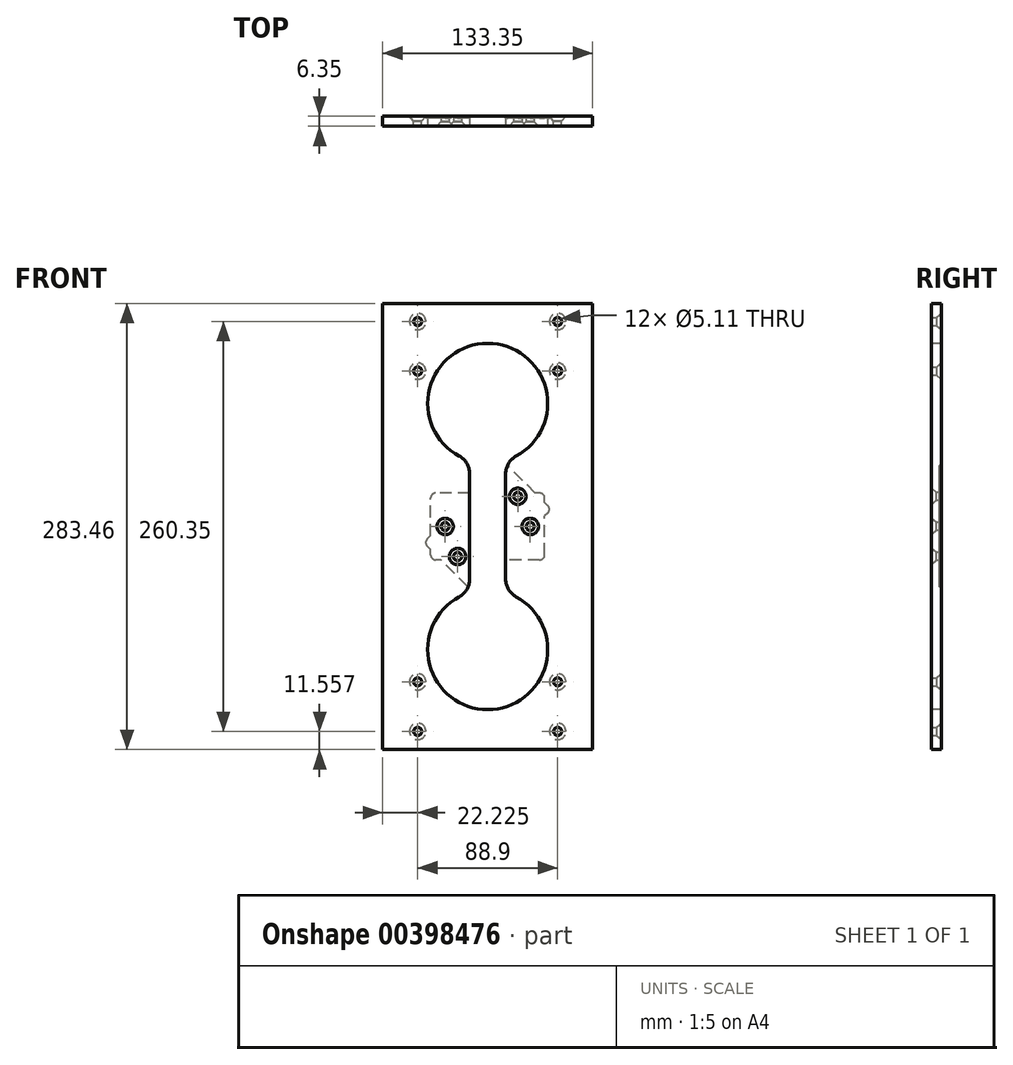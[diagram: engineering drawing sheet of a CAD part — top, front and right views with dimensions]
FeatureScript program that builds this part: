
annotation { "Feature Type Name" : "Feature", "Feature Type Description" : "" }
export const myFeature = defineFeature(function(context is Context, id is Id, definition is map)
    precondition{}
    {
        {
            var Q0;
            Q0=qCreatedBy(makeId("Top.planeOp"),FACE);
            var sketch = newSketch(context, id + "F0", { "sketchPlane" : qUnion([Q0])});
            skLineSegment(sketch, "E0.bottom", {"start": v(0, 0) * mm, "end": v(133.35, 0) * mm});
            skLineSegment(sketch, "E0.top", {"start": v(0, 6.35) * mm, "end": v(133.35, 6.35) * mm});
            skLineSegment(sketch, "E0.left", {"start": v(0, 0) * mm, "end": v(0, 6.35) * mm});
            skLineSegment(sketch, "E0.right", {"start": v(133.35, 0) * mm, "end": v(133.35, 6.35) * mm});
            skSolve(sketch);
        }
        {
            var Q0;
            Q0 = qSketchRegion(id + "F0", true);
            extrude(context, id + "F1", {"entities" : qUnion([Q0]), "depth" : 283.46 * mm});
        }
        {
            var Q0;
            Q0=qCreatedBy(makeId("Top.planeOp"),FACE);
            cPlane(context, id + "F2", {"entities" : qUnion([Q0]), "cplaneType" : CPlaneType.OFFSET, "offset" : ((10.25 + 2 * .455) / 2) * mm, "width" : 152.4 * mm, "height" : 152.4 * mm});
        }
        {
            var Q0;
            Q0=makeQuery(id+"F1.opExtrude","SWEPT_FACE",FACE,{"disambiguationData":[OSD([sQuery(id+"F0.wireOp",EDGE,"E0.bottom")])]});
            var sketch = newSketch(context, id + "F3", { "sketchPlane" : qUnion([Q0])});
            skPoint(sketch, "E1", {"position": v(111.13, 11.56) * mm});
            skPoint(sketch, "E2", {"position": v(22.23, 11.56) * mm});
            skPoint(sketch, "E3", {"position": v(111.13, 271.9) * mm});
            skPoint(sketch, "E4", {"position": v(22.22, 271.9) * mm});
            skLineSegment(sketch, "E5", {"start": v(111.13, 271.9) * mm, "end": v(111.13, 11.56) * mm, "construction": true});
            skLineSegment(sketch, "E6", {"start": v(22.23, 11.56) * mm, "end": v(22.22, 271.9) * mm, "construction": true});
            skPoint(sketch, "E7", {"position": v(111.13, 43.05) * mm});
            skPoint(sketch, "E8", {"position": v(22.23, 43.05) * mm});
            skPoint(sketch, "E9", {"position": v(111.13, 240.41) * mm});
            skPoint(sketch, "E10", {"position": v(22.22, 240.41) * mm});
            skSolve(sketch);
        }
        {
            var Q0;
            {var subQ0=sQuery(id+"F0.wireOp",EDGE,"E0.bottom");Q0=makeQuery(id+"F3.imprint","IMPRINT",FACE,{"disambiguationData":[TD([[makeQuery(id+"F3.imprint","IMPRINT",EDGE,{"derivedFrom":makeQuery(id+"F1.opExtrude","CAP_EDGE",EDGE,{"disambiguationData":[OSD([subQ0])],"isStart":true})}),1.0]])]});}
            var sketch = newSketch(context, id + "F4", { "sketchPlane" : qUnion([Q0])});
            skLineSegment(sketch, "E11.bottom", {"start": v(33.4, 162.43) * mm, "end": v(99.95, 162.43) * mm, "construction": true});
            skLineSegment(sketch, "E11.top", {"start": v(33.4, 121.03) * mm, "end": v(99.95, 121.03) * mm, "construction": true});
            skLineSegment(sketch, "E11.left", {"start": v(31.12, 160.4) * mm, "end": v(31.12, 123.06) * mm, "construction": true});
            skLineSegment(sketch, "E11.right", {"start": v(102.24, 160.4) * mm, "end": v(102.24, 123.06) * mm, "construction": true});
            skLineSegment(sketch, "E12", {"start": v(99.95, 162.43) * mm, "end": v(102.24, 160.4) * mm, "construction": true});
            skLineSegment(sketch, "E13", {"start": v(102.23, 123.06) * mm, "end": v(99.95, 121.03) * mm, "construction": true});
            skLineSegment(sketch, "E14", {"start": v(31.12, 123.06) * mm, "end": v(33.4, 121.03) * mm, "construction": true});
            skLineSegment(sketch, "E15", {"start": v(31.12, 160.4) * mm, "end": v(33.4, 162.43) * mm, "construction": true});
            skLineSegment(sketch, "E16", {"start": v(0, 141.73) * mm, "end": v(133.35, 141.73) * mm, "construction": true});
            skLineSegment(sketch, "E17", {"start": v(66.68, 121.03) * mm, "end": v(66.68, 162.43) * mm, "construction": true});
            skPoint(sketch, "E18", {"position": v(39.66, 141.73) * mm});
            skPoint(sketch, "E19", {"position": v(93.7, 141.73) * mm});
            skPoint(sketch, "E20.1.0", {"position": v(47.57, 122.63) * mm});
            skPoint(sketch, "E20.1.1", {"position": v(85.78, 160.84) * mm});
            skPoint(sketch, "E20.center", {"position": v(66.68, 141.73) * mm});
            skLineSegment(sketch, "E20.anchor1", {"start": v(66.68, 141.73) * mm, "end": v(39.66, 141.73) * mm, "construction": true});
            skLineSegment(sketch, "E20.anchor2", {"start": v(66.68, 141.73) * mm, "end": v(47.57, 122.63) * mm, "construction": true});
            skSolve(sketch);
        }
        {
            var Q0;
            Q0=makeQuery(id+"F1.opExtrude","SWEPT_FACE",FACE,{"disambiguationData":[OSD([sQuery(id+"F0.wireOp",EDGE,"E0.top")])]});
            var sketch = newSketch(context, id + "F5", { "sketchPlane" : qUnion([Q0])});
            skLineSegment(sketch, "E21.bottom", {"start": v(-99.7, 120.52) * mm, "end": v(-75.08, 120.52) * mm});
            skLineSegment(sketch, "E21.top", {"start": v(-99.7, 162.94) * mm, "end": v(-96.89, 162.94) * mm});
            skLineSegment(sketch, "E21.left", {"start": v(-102.87, 123.7) * mm, "end": v(-102.87, 148.31) * mm});
            skLineSegment(sketch, "E21.right", {"start": v(-30.48, 123.7) * mm, "end": v(-30.48, 126.97) * mm});
            skPoint(sketch, "E22.visualSharp", {"position": v(-102.87, 162.94) * mm});
            skArc(sketch, "E22.filletArc", {"start": v(-99.7, 162.94) * mm, "mid": v(-101.94, 162.01) * mm, "end": v(-102.87, 159.77) * mm});
            skArc(sketch, "E23.filletArc", {"start": v(-102.87, 123.7) * mm, "mid": v(-101.94, 121.45) * mm, "end": v(-99.7, 120.52) * mm});
            skPoint(sketch, "E24.visualSharp", {"position": v(-30.48, 162.94) * mm});
            skArc(sketch, "E24.filletArc", {"start": v(-30.48, 159.77) * mm, "mid": v(-31.4, 162.01) * mm, "end": v(-33.66, 162.94) * mm});
            skArc(sketch, "E25.filletArc", {"start": v(-33.66, 120.52) * mm, "mid": v(-31.4, 121.45) * mm, "end": v(-30.48, 123.7) * mm});
            skPoint(sketch, "E26", {"position": v(-66.27, 141.8) * mm});
            skLineSegment(sketch, "E27.1.0", {"start": v(-74.95, 180.38) * mm, "end": v(-57.51, 162.94) * mm});
            skLineSegment(sketch, "E27.1.1", {"start": v(-53.76, 103.7) * mm, "end": v(-36.93, 120.52) * mm});
            skPoint(sketch, "E27.1.2", {"position": v(-77.2, 182.63) * mm});
            skLineSegment(sketch, "E27.1.3", {"start": v(-104.95, 154.88) * mm, "end": v(-102.87, 156.96) * mm});
            skPoint(sketch, "E27.1.5", {"position": v(-26.01, 131.44) * mm});
            skLineSegment(sketch, "E27.1.6", {"start": v(-104.95, 150.39) * mm, "end": v(-102.87, 148.31) * mm});
            skArc(sketch, "E27.1.7", {"start": v(-104.95, 154.88) * mm, "mid": v(-105.88, 152.63) * mm, "end": v(-104.95, 150.39) * mm});
            skArc(sketch, "E27.1.8", {"start": v(-58.25, 103.7) * mm, "mid": v(-56, 102.76) * mm, "end": v(-53.76, 103.7) * mm});
            skArc(sketch, "E27.1.9", {"start": v(-74.95, 180.38) * mm, "mid": v(-77.2, 181.31) * mm, "end": v(-79.44, 180.38) * mm});
            skArc(sketch, "E27.1.10", {"start": v(-28.26, 129.2) * mm, "mid": v(-27.33, 131.44) * mm, "end": v(-28.26, 133.69) * mm});
            skLineSegment(sketch, "E27.anchor1", {"start": v(-66.27, 141.8) * mm, "end": v(-99.7, 120.52) * mm, "construction": true});
            skLineSegment(sketch, "E27.anchor2", {"start": v(-66.27, 141.8) * mm, "end": v(-104.95, 150.39) * mm, "construction": true});
            skLineSegment(sketch, "E28.trimOffspring", {"start": v(-57.51, 162.94) * mm, "end": v(-33.66, 162.94) * mm});
            skLineSegment(sketch, "E29.trimOffspring", {"start": v(-30.48, 135.91) * mm, "end": v(-28.26, 133.69) * mm});
            skLineSegment(sketch, "E30.trimOffspring", {"start": v(-30.48, 135.91) * mm, "end": v(-30.48, 159.77) * mm});
            skLineSegment(sketch, "E31.trimOffspring", {"start": v(-36.93, 120.52) * mm, "end": v(-33.66, 120.52) * mm});
            skLineSegment(sketch, "E32.trimOffspring", {"start": v(-30.48, 126.97) * mm, "end": v(-28.26, 129.2) * mm});
            skLineSegment(sketch, "E33.trimOffspring", {"start": v(-75.08, 120.52) * mm, "end": v(-58.25, 103.7) * mm});
            skLineSegment(sketch, "E34.trimOffspring", {"start": v(-102.87, 156.96) * mm, "end": v(-102.87, 159.77) * mm});
            skLineSegment(sketch, "E35.trimOffspring", {"start": v(-96.89, 162.94) * mm, "end": v(-79.44, 180.38) * mm});
            skSolve(sketch);
        }
        {
            var Q0;
            Q0 = qSketchRegion(id + "F5", true);
            extrude(context, id + "F6", {"entities" : qUnion([Q0]), "operationType" : NewBodyOperationType.REMOVE, "oppositeDirection" : true, "depth" : 1.27 * mm});
        }
        {
            var Q0;
            Q0=sQuery(id+"F4.wireOp",VERTEX,"E18");
            var Q1;
            Q1=sQuery(id+"F4.wireOp",VERTEX,"E19");
            var Q2;
            Q2=sQuery(id+"F4.wireOp",VERTEX,"E20.1.1");
            var Q3;
            Q3=sQuery(id+"F4.wireOp",VERTEX,"E20.1.0");
            var Q4;
            Q4=makeQuery(id+"F1.opExtrude","SWEPT_BODY",BODY,{"disambiguationData":[OSD([sQuery(id+"F0.wireOp",EDGE,"E0.bottom"),sQuery(id+"F0.wireOp",EDGE,"E0.top"),sQuery(id+"F0.wireOp",EDGE,"E0.left"),sQuery(id+"F0.wireOp",EDGE,"E0.right")])]});
            hole(context, id + "F7", {"style" : HoleStyle.C_SINK, "endStyle" : HoleEndStyle.THROUGH, "standardTappedOrClearance" : lookupTablePath({ "standard" : "ANSI", "fit" : "Normal (ASME)", "size" : "#10", "type" : "Clearance" }), "standardBlindInLast" : lookupTablePath({ "fit" : "Free", "standard" : "ANSI", "size" : "#10", "type" : "Clearance" }), "holeDiameter" : 5.1 * mm, "cSinkDiameter" : 10.44 * mm, "cSinkAngle" : 82 * degree, "isTappedThrough" : true, "tappedDepth" : 12.7 * mm, "tapClearance" : 3, "locations" : qUnion([Q0, Q1, Q2, Q3]), "scope" : qUnion([Q4])});
        }
        {
            var Q0;
            Q0=makeQuery(id+"F1.opExtrude","SWEPT_FACE",FACE,{"disambiguationData":[OSD([sQuery(id+"F0.wireOp",EDGE,"E0.top")])]});
            var sketch = newSketch(context, id + "F8", { "sketchPlane" : qUnion([Q0])});
            skPoint(sketch, "E36", {"position": v(-22.22, 271.9) * mm});
            skPoint(sketch, "E37", {"position": v(-111.13, 271.9) * mm});
            skPoint(sketch, "E38", {"position": v(-22.23, 11.56) * mm});
            skPoint(sketch, "E39", {"position": v(-111.13, 11.56) * mm});
            skPoint(sketch, "E40", {"position": v(-111.13, 240.41) * mm});
            skPoint(sketch, "E41", {"position": v(-22.22, 240.41) * mm});
            skPoint(sketch, "E42", {"position": v(-22.23, 43.05) * mm});
            skPoint(sketch, "E43", {"position": v(-111.13, 43.05) * mm});
            skSolve(sketch);
        }
        {
            var Q0;
            Q0=sQuery(id+"F8.wireOp",VERTEX,"E36");
            var Q1;
            Q1=sQuery(id+"F8.wireOp",VERTEX,"E37");
            var Q2;
            Q2=sQuery(id+"F8.wireOp",VERTEX,"E38");
            var Q3;
            Q3=sQuery(id+"F8.wireOp",VERTEX,"E39");
            var Q4;
            Q4=sQuery(id+"F8.wireOp",VERTEX,"E40");
            var Q5;
            Q5=sQuery(id+"F8.wireOp",VERTEX,"E41");
            var Q6;
            Q6=sQuery(id+"F8.wireOp",VERTEX,"E43");
            var Q7;
            Q7=sQuery(id+"F8.wireOp",VERTEX,"E42");
            var Q8;
            Q8=makeQuery(id+"F1.opExtrude","SWEPT_BODY",BODY,{"disambiguationData":[OSD([sQuery(id+"F0.wireOp",EDGE,"E0.bottom"),sQuery(id+"F0.wireOp",EDGE,"E0.top"),sQuery(id+"F0.wireOp",EDGE,"E0.left"),sQuery(id+"F0.wireOp",EDGE,"E0.right")])]});
            hole(context, id + "F9", {"style" : HoleStyle.C_SINK, "endStyle" : HoleEndStyle.THROUGH, "standardTappedOrClearance" : lookupTablePath({ "standard" : "ANSI", "fit" : "Normal (ASME)", "size" : "#10", "type" : "Clearance" }), "standardBlindInLast" : lookupTablePath({ "fit" : "Free", "standard" : "ANSI", "size" : "#10", "type" : "Clearance" }), "holeDiameter" : 5.1 * mm, "cSinkDiameter" : 10.44 * mm, "cSinkAngle" : 82 * degree, "isTappedThrough" : true, "tappedDepth" : 12.7 * mm, "tapClearance" : 3, "locations" : qUnion([Q0, Q1, Q2, Q3, Q4, Q5, Q6, Q7]), "scope" : qUnion([Q8])});
        }
        {
            var Q0;
            {var subQ0=sQuery(id+"F0.wireOp",EDGE,"E0.bottom");Q0=makeQuery(id+"F3.imprint","IMPRINT",FACE,{"disambiguationData":[TD([[makeQuery(id+"F3.imprint","IMPRINT",EDGE,{"derivedFrom":makeQuery(id+"F1.opExtrude","CAP_EDGE",EDGE,{"disambiguationData":[OSD([subQ0])],"isStart":true})}),1.0]])]});}
            var sketch = newSketch(context, id + "F10", { "sketchPlane" : qUnion([Q0])});
            skLineSegment(sketch, "E44.bottom", {"start": v(92.07, 241.74) * mm, "end": v(41.27, 241.74) * mm, "construction": true});
            skLineSegment(sketch, "E44.top", {"start": v(92.08, 41.72) * mm, "end": v(41.28, 41.72) * mm, "construction": true});
            skLineSegment(sketch, "E44.left", {"start": v(92.07, 241.74) * mm, "end": v(92.08, 41.72) * mm, "construction": true});
            skLineSegment(sketch, "E44.right", {"start": v(41.27, 241.74) * mm, "end": v(41.28, 41.72) * mm, "construction": true});
            skLineSegment(sketch, "E45", {"start": v(41.28, 141.73) * mm, "end": v(0, 141.73) * mm, "construction": true});
            skLineSegment(sketch, "E46", {"start": v(66.67, 241.74) * mm, "end": v(66.67, 283.46) * mm, "construction": true});
            skLineSegment(sketch, "E47.bottom", {"start": v(81.28, 63.3) * mm, "end": v(52.07, 63.3) * mm, "construction": true});
            skLineSegment(sketch, "E47.top", {"start": v(81.28, 134.43) * mm, "end": v(52.07, 134.43) * mm, "construction": true});
            skLineSegment(sketch, "E47.left", {"start": v(81.28, 63.3) * mm, "end": v(81.28, 134.43) * mm, "construction": true});
            skLineSegment(sketch, "E47.right", {"start": v(52.07, 63.3) * mm, "end": v(52.07, 134.43) * mm, "construction": true});
            skArc(sketch, "E48", {"start": v(84.77, 186.44) * mm, "mid": v(66.68, 258.06) * mm, "end": v(48.58, 186.44) * mm});
            skLineSegment(sketch, "E49", {"start": v(66.67, 283.46) * mm, "end": v(66.67, 0) * mm, "construction": true});
            skArc(sketch, "E50", {"start": v(48.58, 97.03) * mm, "mid": v(66.68, 25.4) * mm, "end": v(84.77, 97.03) * mm});
            skLineSegment(sketch, "E51", {"start": v(78.1, 175.26) * mm, "end": v(78.1, 108.2) * mm});
            skLineSegment(sketch, "E52", {"start": v(55.24, 175.26) * mm, "end": v(55.25, 108.2) * mm});
            skPoint(sketch, "E53.visualSharp", {"position": v(78.1, 183.62) * mm});
            skArc(sketch, "E53.filletArc", {"start": v(84.77, 186.44) * mm, "mid": v(79.9, 181.77) * mm, "end": v(78.1, 175.26) * mm});
            skPoint(sketch, "E54.visualSharp", {"position": v(55.24, 183.62) * mm});
            skArc(sketch, "E54.filletArc", {"start": v(55.24, 175.26) * mm, "mid": v(53.45, 181.77) * mm, "end": v(48.58, 186.44) * mm});
            skPoint(sketch, "E55.visualSharp", {"position": v(55.25, 99.85) * mm});
            skArc(sketch, "E55.filletArc", {"start": v(48.58, 97.03) * mm, "mid": v(53.45, 101.7) * mm, "end": v(55.25, 108.2) * mm});
            skPoint(sketch, "E56.visualSharp", {"position": v(78.1, 99.85) * mm});
            skArc(sketch, "E56.filletArc", {"start": v(78.1, 108.2) * mm, "mid": v(79.9, 101.7) * mm, "end": v(84.77, 97.03) * mm});
            skSolve(sketch);
        }
        {
            var Q0;
            Q0 = qSketchRegion(id + "F10", true);
            extrude(context, id + "F11", {"entities" : qUnion([Q0]), "operationType" : NewBodyOperationType.REMOVE, "endBound" : BoundingType.THROUGH_ALL, "oppositeDirection" : true, "depth" : 25.4 * mm});
        }
    });
